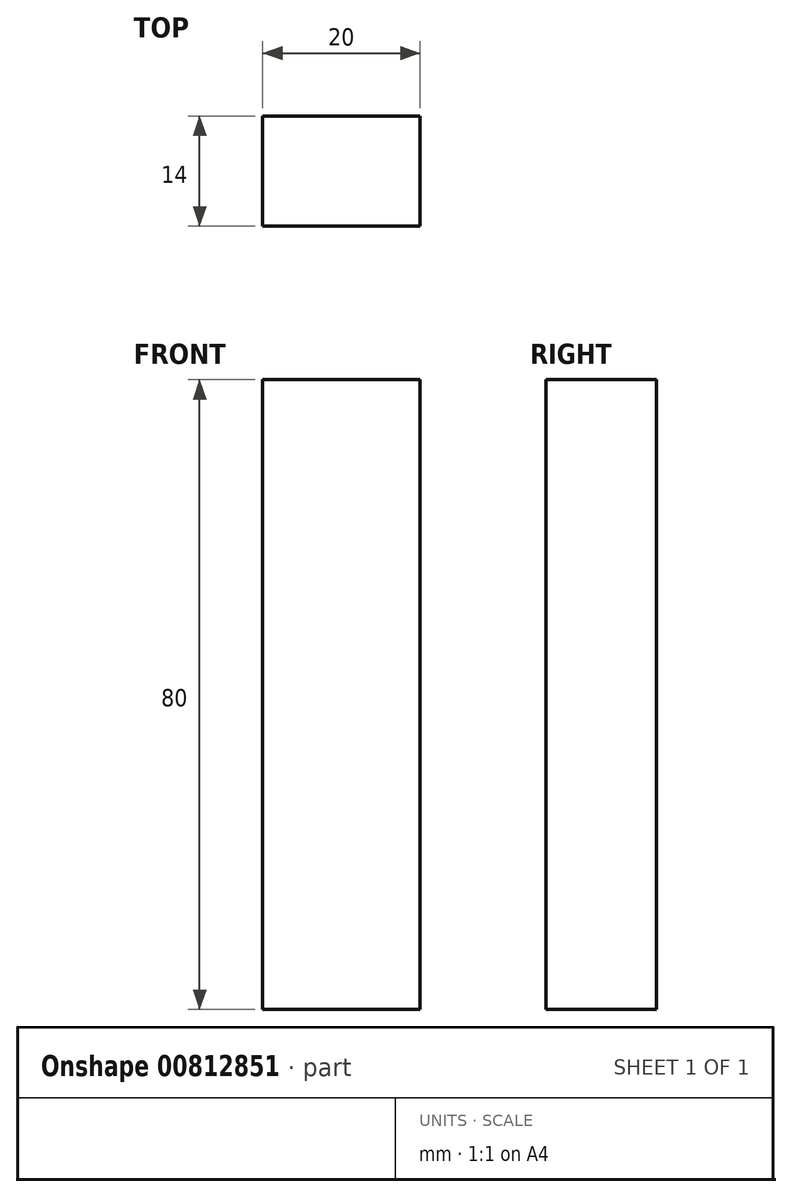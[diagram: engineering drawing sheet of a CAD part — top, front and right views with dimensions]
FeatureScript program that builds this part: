
annotation { "Feature Type Name" : "Feature", "Feature Type Description" : "" }
export const myFeature = defineFeature(function(context is Context, id is Id, definition is map)
    precondition{}
    {
        {
            var Q0;
            Q0=qCreatedBy(makeId("Top.planeOp"),FACE);
            var sketch = newSketch(context, id + "F0", { "sketchPlane" : qUnion([Q0])});
            skLineSegment(sketch, "E0.bottom", {"start": v(-5.46, 7.42) * mm, "end": v(14.54, 7.42) * mm});
            skLineSegment(sketch, "E0.top", {"start": v(-5.46, -6.58) * mm, "end": v(14.54, -6.58) * mm});
            skLineSegment(sketch, "E0.left", {"start": v(-5.46, 7.42) * mm, "end": v(-5.46, -6.58) * mm});
            skLineSegment(sketch, "E0.right", {"start": v(14.54, 7.42) * mm, "end": v(14.54, -6.58) * mm});
            skSolve(sketch);
        }
        {
            var Q0;
            Q0=makeQuery(id+"F0.imprint","IMPRINT",FACE,{"disambiguationData":[TD([[makeQuery(id+"F0.imprint","IMPRINT",EDGE,{"derivedFrom":sQuery(id+"F0.wireOp",EDGE,"E0.bottom")}),-1.0]])]});
            extrude(context, id + "F1", {"entities" : qUnion([Q0]), "depth" : 80 * mm, "offsetDistance" : 25 * mm});
        }
    });
